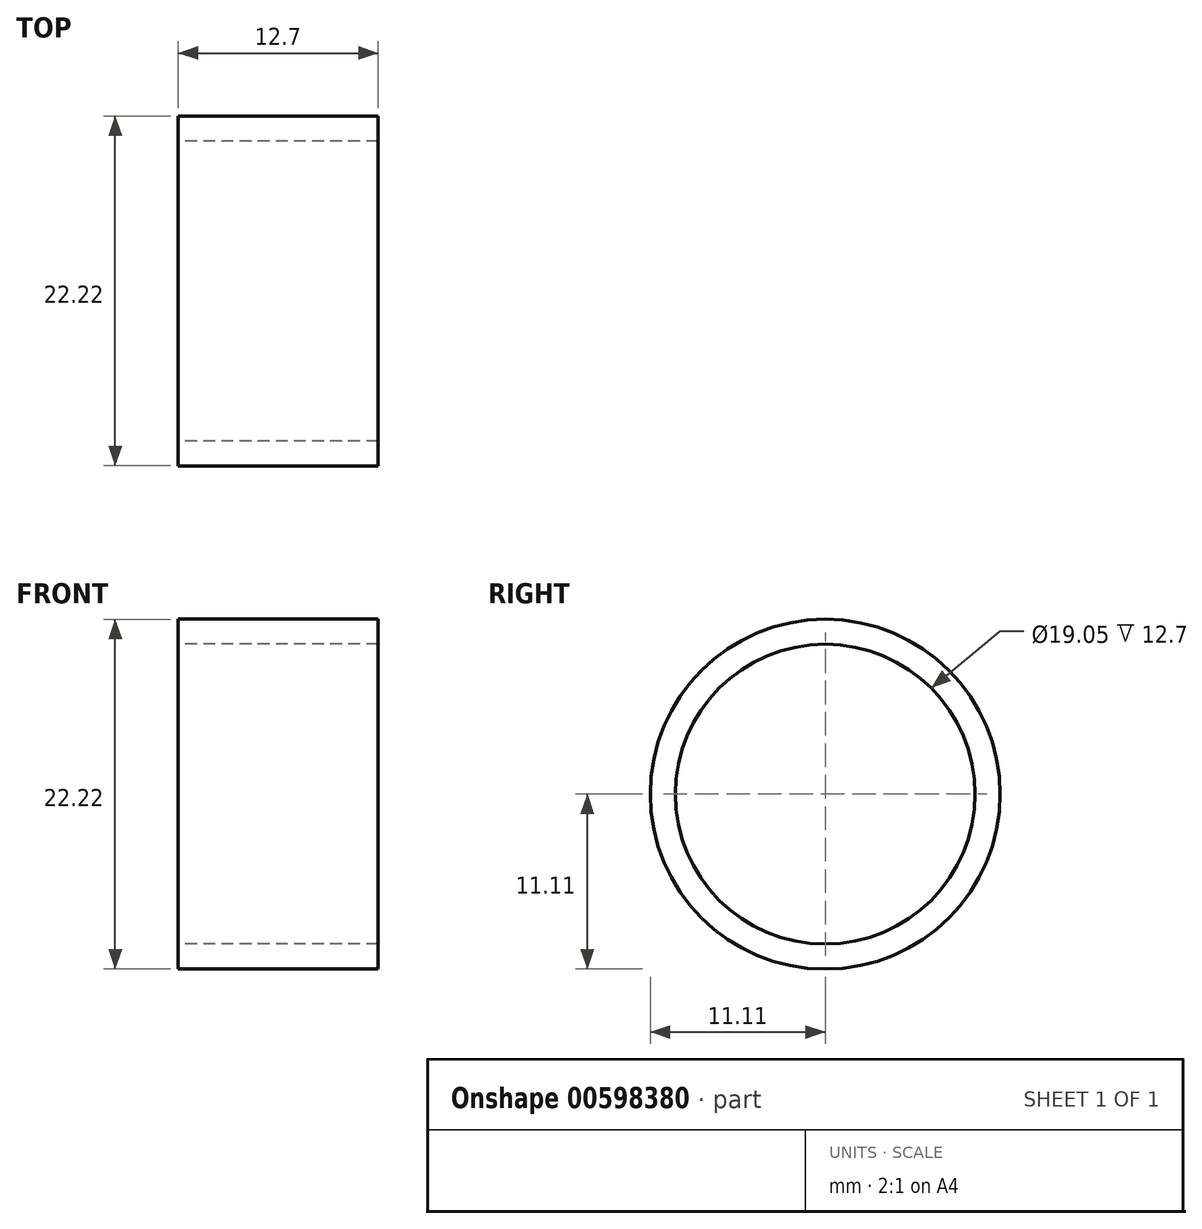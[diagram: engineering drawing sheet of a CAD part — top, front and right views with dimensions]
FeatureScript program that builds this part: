
annotation { "Feature Type Name" : "Feature", "Feature Type Description" : "" }
export const myFeature = defineFeature(function(context is Context, id is Id, definition is map)
    precondition{}
    {
        {
            var Q0;
            Q0=qCreatedBy(makeId("Right.planeOp"),FACE);
            var sketch = newSketch(context, id + "F0", { "sketchPlane" : qUnion([Q0])});
            skCircle(sketch, "E0", {"center": v(0, 0) * mm, "radius": 9.53 * mm});
            skCircle(sketch, "E1", {"center": v(0, 0) * mm, "radius": 11.11 * mm});
            skSolve(sketch);
        }
        {
            var Q0;
            Q0 = qSketchRegion(id + "F0", true);
            extrude(context, id + "F1", {"entities" : qUnion([Q0]), "depth" : 12.7 * mm, "offsetDistance" : 25.4 * mm});
        }
    });
